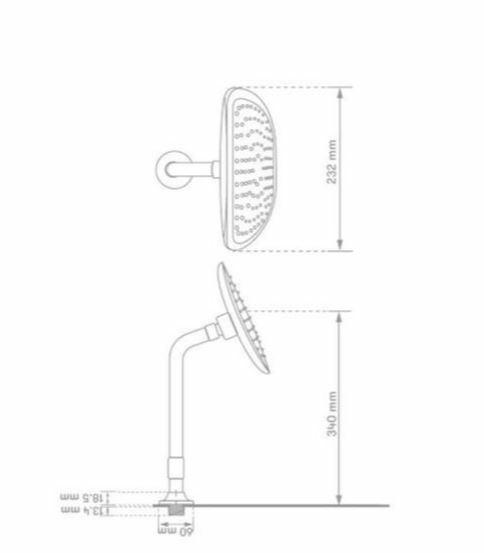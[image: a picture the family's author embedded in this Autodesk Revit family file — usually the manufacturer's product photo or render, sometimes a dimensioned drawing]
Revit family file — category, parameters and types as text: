
# Revit family: 01-0935-11 MEZCLADOR DUCHA 8 SST HELVETIA
name_source: partatom
category: Aparatos sanitarios
revit_build: Autodesk Revit 2018 (Build: 20170223_1515(x64)
units: mm (PartAtom-declared; Revit-internal decimal feet)

## family parameters
Anfitrión = Cara
Compartido = No
Corte con vacíos al cargar = No
Cota de conector redondo = Diámetro de uso
Número OmniClass = 23.31.11.00
Punto de cálculo de habitación = No
Tipo de pieza = Normal

## types (1)
- 01-0935-11
    Alto = 60 mm  [stored 0.19685 ft]
    Ancho = 60 mm  [stored 0.19685 ft]
    Conexión AC = Sí
    Conexión AF = Sí
    Conexión de residuos = No
    Conexión de ventilación = No
    Descripción = Mezclador ducha
    Distancia entre griferias = 203 mm
    Elevación por defecto = 0 mm  [stored 0 ft]
    Fabricante = Gricol
    Imagen de tipo = <Ninguno>
    Link Ficha Tecnica = https://infotecnica.gricol.com
    Metal Acero Inoxidable Cromado = Metal Acero Inoxidable Cromado
    Metal Laton Cromado = Metal Laton Cromado
    Mezclador = Mezclador
    Modelo = 01-0935-11
    Plastico ABS Cromado = Plastico ABS Cromado
    Product Name = MEZCLADOR DUCHA 8 SST HELVETIA
    Profundidad = 85 mm  [stored 0.278871 ft]
    Sepacion entre registro y ducha = 400 mm  [stored 1.31234 ft]
    URL = https://www.gricol.com

note: [stored X ft] marks values corroborated as IEEE doubles in the binary element streams (Revit-internal decimal feet)

## geometry (parser evidence)
native form markers: Blend x2, Sweep x30
no freeform markers — native parametric forms only
